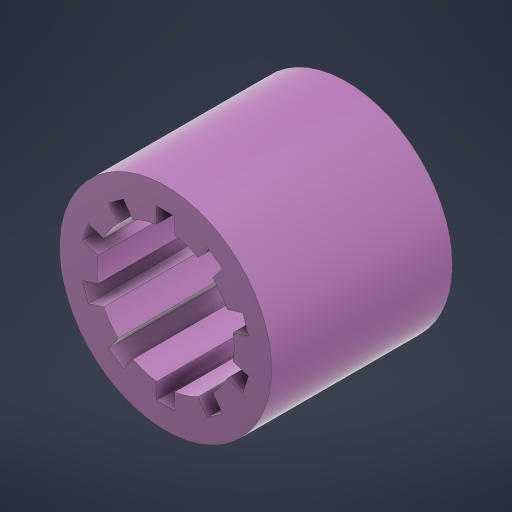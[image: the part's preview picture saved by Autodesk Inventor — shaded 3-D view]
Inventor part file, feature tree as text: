
AUTODESK INVENTOR PART (.ipt)
format: ipt  version: 2024 (Build 280153000, 153)  size: 275,456 bytes
history: native  units: in
note: dims shown in document units (in); Inventor stores cm internally (conversion verified against a paired STEP export)
features: extrude x1, sketch x1
ambient origin geometry x8: Origin, YZ Plane, XZ Plane, XY Plane, X Axis, Y Axis, Z Axis, Center Point
bodies: Solid1 (feature_tree)
feature tree (2):
  extrude  "Extrusion1"  Depth=0.1138in
  sketch  "Sketch1"  dims[d1=3.937in d2=360.0deg d3=1.3386in d4=1.1417in d5=0.0in d6=0.4331in d7=0.6693in d8=0.1021in d9=0.1138in]
